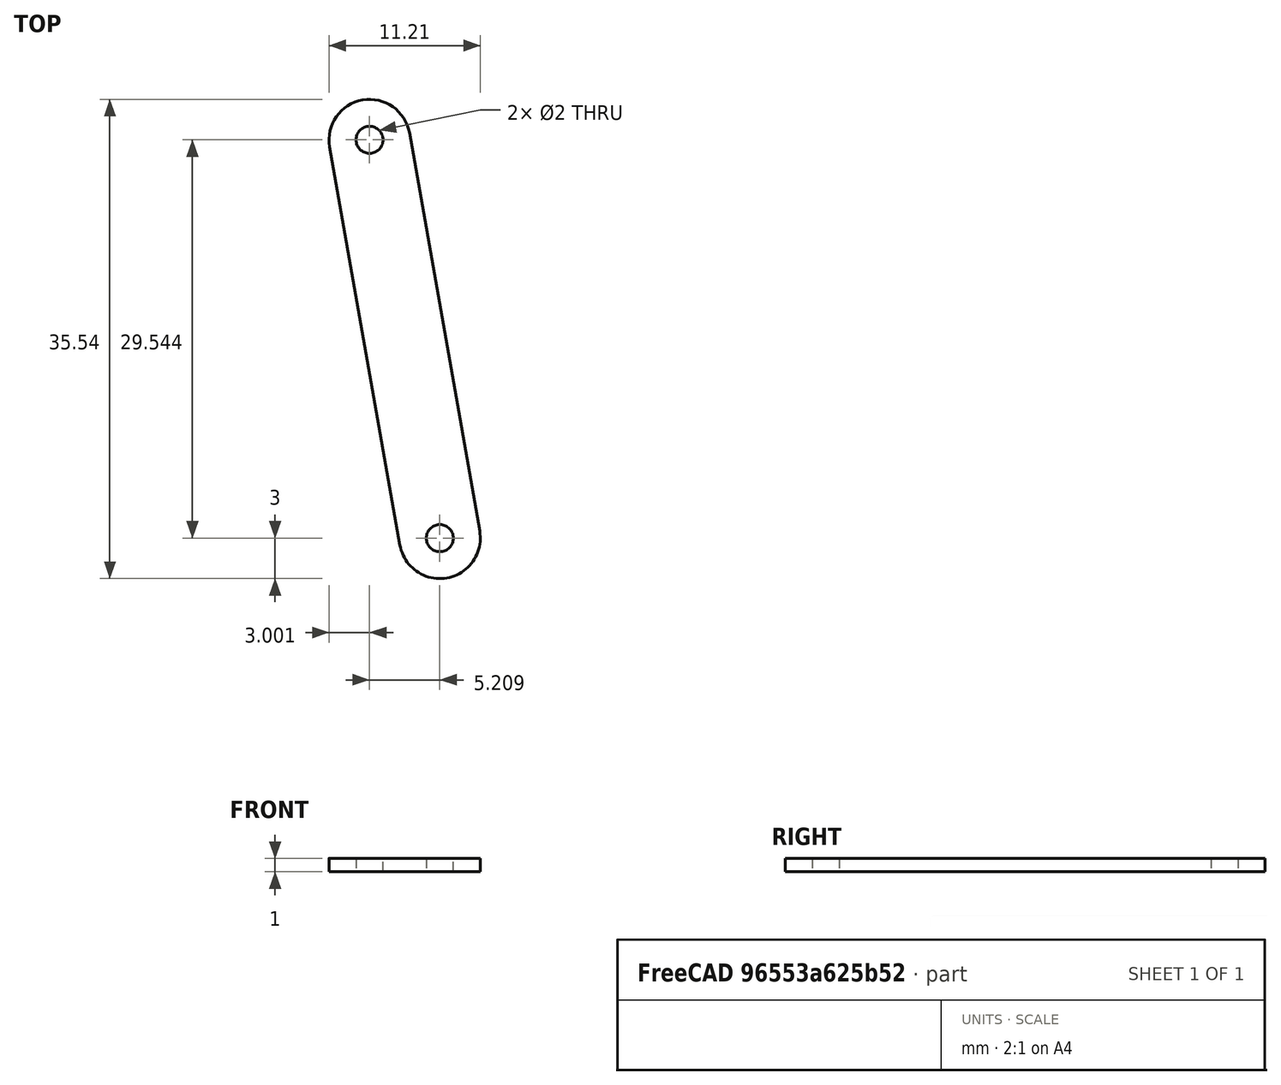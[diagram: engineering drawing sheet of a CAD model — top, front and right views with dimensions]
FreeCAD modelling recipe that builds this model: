
FCSTD DOCUMENT  (FreeCAD 0.19R24276 (Git))
Label: Right
License: All rights reserved
LicenseURL: http://en.wikipedia.org/wiki/All_rights_reserved
objects: Sketcher::SketchObject×1, PartDesign::Pad×1, PartDesign::Body×1
note: 4 computed .brp shape members not serialized (recipe doc carries the construction recipe); baked Part::Feature solids carry a one-line shape summary decoded from their .brp

FEATURE [Sketcher::SketchObject] Sketch
  FullyConstrained = true
  MapMode = 5
  Support = -> [XY_Plane]
  sketch-geometry (7):
    g0: ArcOfCircle CenterX=-5.20945 CenterY=29.5442 CenterZ=0 NormalX=0 NormalY=0 NormalZ=1 AngleXU=0 Radius=3 StartAngle=0.174533 EndAngle=3.31613
    g1: ArcOfCircle CenterX=0 CenterY=0 CenterZ=0 NormalX=0 NormalY=0 NormalZ=1 AngleXU=0 Radius=3 StartAngle=3.31613 EndAngle=6.45772
    g2: LineSegment StartX=-8.16387 StartY=29.0233 StartZ=0 EndX=-2.95442 EndY=-0.520945 EndZ=0
    g3: LineSegment StartX=-2.25502 StartY=30.0652 StartZ=0 EndX=2.95442 EndY=0.520945 EndZ=0
    g4: Circle CenterX=-5.20945 CenterY=29.5442 CenterZ=0 NormalX=0 NormalY=0 NormalZ=1 AngleXU=0 Radius=1
    g5: Circle CenterX=0 CenterY=0 CenterZ=0 NormalX=0 NormalY=0 NormalZ=1 AngleXU=0 Radius=1
    g6: LineSegment StartX=-5.20945 StartY=29.5442 StartZ=0 EndX=0 EndY=0 EndZ=0
  constraints (15):
    c: Tangent(g0,g3) = 1.5708
    c: Tangent(g0,g2) = -1.5708
    c: Tangent(g2,g1) = -1.5708
    c: Tangent(g3,g1) = 1.5708
    c: Equal(g0,g1)
    c: Coincident(g4,g0)
    c: Coincident(g5,g1)
    c: Radius(g4) = 1
    c: Radius(g5) = 1
    c: Radius(g1) = 3
    c: Coincident(g1,g-1)
    c: Coincident(g6,g0)
    c: Coincident(g6,g1)
    c: Angle(g-2,g6) = 0.174533
    c: Distance(g6) = 30
FEATURE [PartDesign::Pad] Pad
  Direction = (1,1,1)
  Length = 1
  Length2 = 100
  Profile = -> Sketch
  Type = 0
FEATURE [PartDesign::Body] Body  label="Right"
  Group = -> [Sketch,Pad]
  Origin = -> Origin
  Tip = -> Pad
